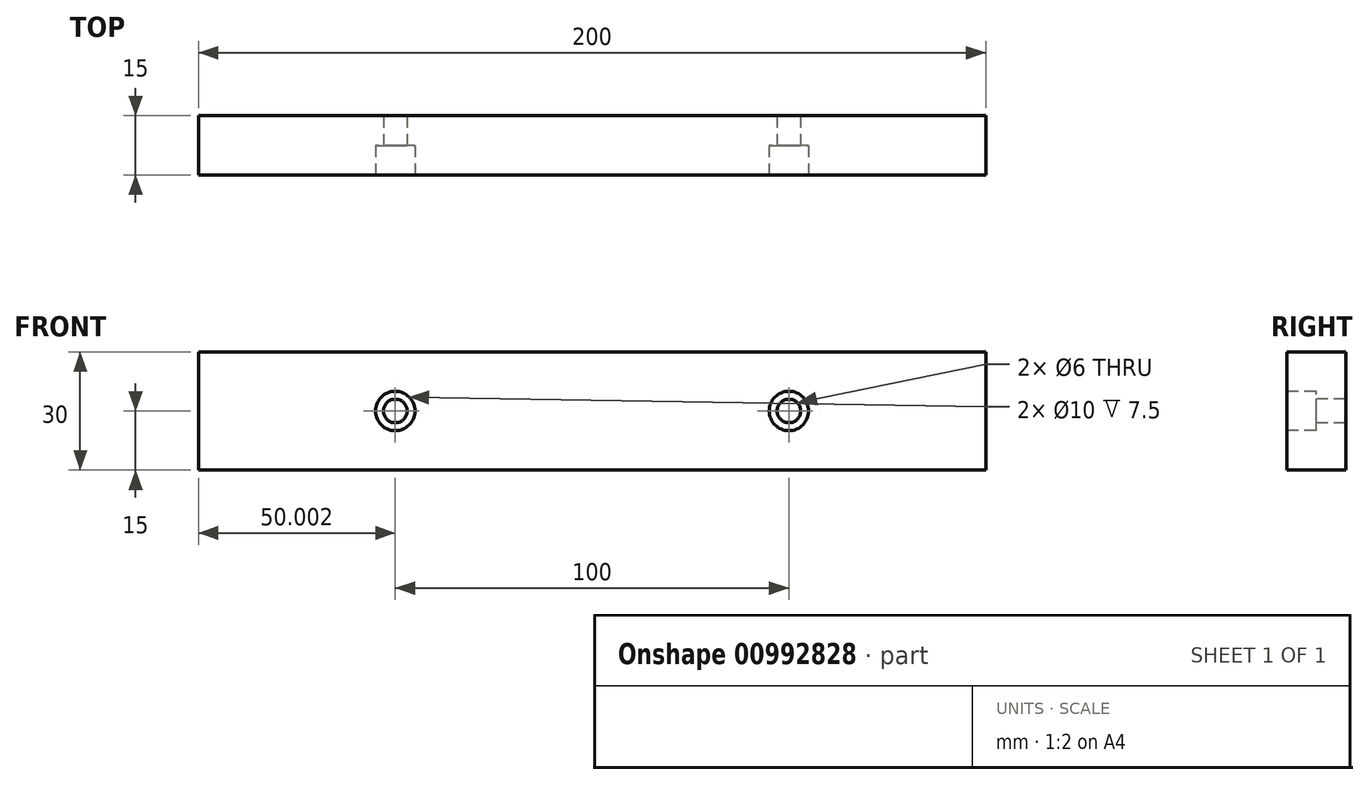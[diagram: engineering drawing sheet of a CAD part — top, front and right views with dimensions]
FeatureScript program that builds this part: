
annotation { "Feature Type Name" : "Feature", "Feature Type Description" : "" }
export const myFeature = defineFeature(function(context is Context, id is Id, definition is map)
    precondition{}
    {
        {
            var Q0;
            Q0=qCreatedBy(makeId("Front.planeOp"),FACE);
            var sketch = newSketch(context, id + "F0", { "sketchPlane" : qUnion([Q0])});
            skLineSegment(sketch, "E0.bottom", {"start": v(-45.6, 30) * mm, "end": v(154.4, 30) * mm});
            skLineSegment(sketch, "E0.top", {"start": v(-45.6, 0) * mm, "end": v(154.4, 0) * mm});
            skLineSegment(sketch, "E0.left", {"start": v(-45.6, 30) * mm, "end": v(-45.6, 0) * mm});
            skLineSegment(sketch, "E0.right", {"start": v(154.4, 30) * mm, "end": v(154.4, 0) * mm});
            skPoint(sketch, "E1.oppositeSnap0", {"position": v(-45.6, 15) * mm});
            skLineSegment(sketch, "E1.left", {"start": v(-45.6, 15) * mm, "end": v(-45.6, 15) * mm});
            skPoint(sketch, "E2.oppositeSnap0", {"position": v(154.4, 15) * mm});
            skLineSegment(sketch, "E2.left", {"start": v(154.4, 15) * mm, "end": v(154.4, 15) * mm});
            skSolve(sketch);
        }
        {
            var Q0;
            Q0=makeQuery(id+"F0.imprint","IMPRINT",FACE,{"disambiguationData":[TD([[makeQuery(id+"F0.imprint","IMPRINT",EDGE,{"derivedFrom":sQuery(id+"F0.wireOp",EDGE,"E0.bottom")}),-1.0]])]});
            extrude(context, id + "F1", {"entities" : qUnion([Q0]), "depth" : 15 * mm, "offsetDistance" : 25 * mm});
        }
        {
            var Q0;
            Q0=makeQuery(id+"F1.opExtrude","CAP_FACE",FACE,{"disambiguationData":[OSD([sQuery(id+"F0.wireOp",EDGE,"E0.bottom"),sQuery(id+"F0.wireOp",EDGE,"E0.top"),sQuery(id+"F0.wireOp",EDGE,"E0.left"),sQuery(id+"F0.wireOp",EDGE,"E0.right")])],"isStart":false});
            var sketch = newSketch(context, id + "F2", { "sketchPlane" : qUnion([Q0])});
            skCircle(sketch, "E3", {"center": v(4.4, 15) * mm, "radius": 5 * mm});
            skCircle(sketch, "E4", {"center": v(4.4, 15) * mm, "radius": 3 * mm});
            skCircle(sketch, "E5", {"center": v(104.4, 15) * mm, "radius": 5 * mm});
            skCircle(sketch, "E6", {"center": v(104.4, 15) * mm, "radius": 3 * mm});
            skSolve(sketch);
        }
        {
            var Q0;
            Q0=makeQuery(id+"F2.imprint","IMPRINT",FACE,{"disambiguationData":[TD([[makeQuery(id+"F2.imprint","IMPRINT",EDGE,{"derivedFrom":sQuery(id+"F2.wireOp",EDGE,"E4")}),1.0]])]});
            var Q1;
            Q1=makeQuery(id+"F2.imprint","IMPRINT",FACE,{"disambiguationData":[TD([[makeQuery(id+"F2.imprint","IMPRINT",EDGE,{"derivedFrom":sQuery(id+"F2.wireOp",EDGE,"E6")}),1.0]])]});
            extrude(context, id + "F3", {"entities" : qUnion([Q0, Q1]), "operationType" : NewBodyOperationType.REMOVE, "oppositeDirection" : true, "depth" : 25 * mm, "offsetDistance" : 25 * mm});
        }
        {
            var Q0;
            Q0 = qSketchRegion(id + "F2", true);
            extrude(context, id + "F4", {"entities" : qUnion([Q0]), "operationType" : NewBodyOperationType.REMOVE, "oppositeDirection" : true, "depth" : 7.5 * mm, "offsetDistance" : 25 * mm});
        }
    });
